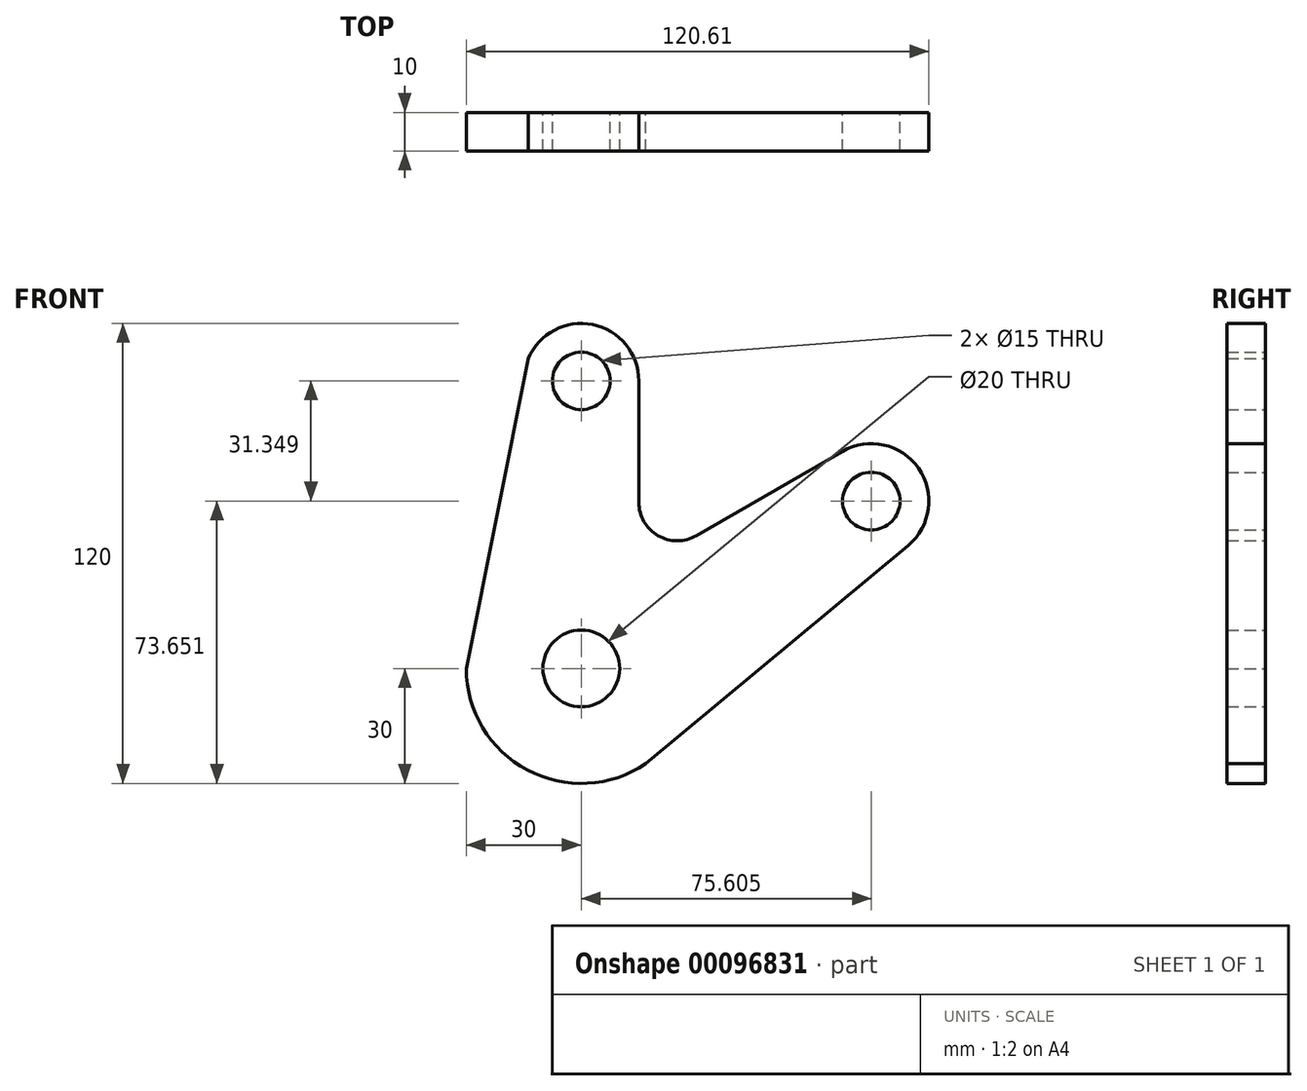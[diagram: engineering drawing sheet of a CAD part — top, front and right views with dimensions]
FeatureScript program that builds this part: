
annotation { "Feature Type Name" : "Feature", "Feature Type Description" : "" }
export const myFeature = defineFeature(function(context is Context, id is Id, definition is map)
    precondition{}
    {
        {
            var Q0;
            Q0=qCreatedBy(makeId("Front.planeOp"),FACE);
            var sketch = newSketch(context, id + "F0", { "sketchPlane" : qUnion([Q0])});
            skCircle(sketch, "E0", {"center": v(0, 0) * mm, "radius": 10 * mm});
            skArc(sketch, "E1", {"start": v(-30, 0) * mm, "mid": v(-14.06, -26.5) * mm, "end": v(16.82, -24.84) * mm});
            skLineSegment(sketch, "E2", {"start": v(0, 0) * mm, "end": v(0, 75) * mm, "construction": true});
            skCircle(sketch, "E3", {"center": v(0, 75) * mm, "radius": 7.5 * mm});
            skLineSegment(sketch, "E4", {"start": v(0, 0) * mm, "end": v(75.6, 43.65) * mm, "construction": true});
            skArc(sketch, "E5", {"start": v(15, 75) * mm, "mid": v(2.98, 89.7) * mm, "end": v(-13.82, 80.84) * mm});
            skLineSegment(sketch, "E6", {"start": v(-13.82, 80.84) * mm, "end": v(-30, 0) * mm});
            skCircle(sketch, "E7", {"center": v(75.6, 43.65) * mm, "radius": 7.5 * mm});
            skArc(sketch, "E8", {"start": v(85.2, 32.13) * mm, "mid": v(87.9, 52.23) * mm, "end": v(68.1, 56.64) * mm});
            skLineSegment(sketch, "E9", {"start": v(16.82, -24.84) * mm, "end": v(85.2, 32.13) * mm});
            skLineSegment(sketch, "E10", {"start": v(15, 75) * mm, "end": v(15, 43.3) * mm});
            skArc(sketch, "E11", {"start": v(15, 43.3) * mm, "mid": v(20, 34.64) * mm, "end": v(30, 34.64) * mm});
            skLineSegment(sketch, "E12", {"start": v(30, 34.64) * mm, "end": v(68.1, 56.64) * mm});
            skSolve(sketch);
        }
        {
            var Q0;
            Q0 = qSketchRegion(id + "F0", true);
            extrude(context, id + "F1", {"entities" : qUnion([Q0]), "depth" : 10 * mm});
        }
    });
